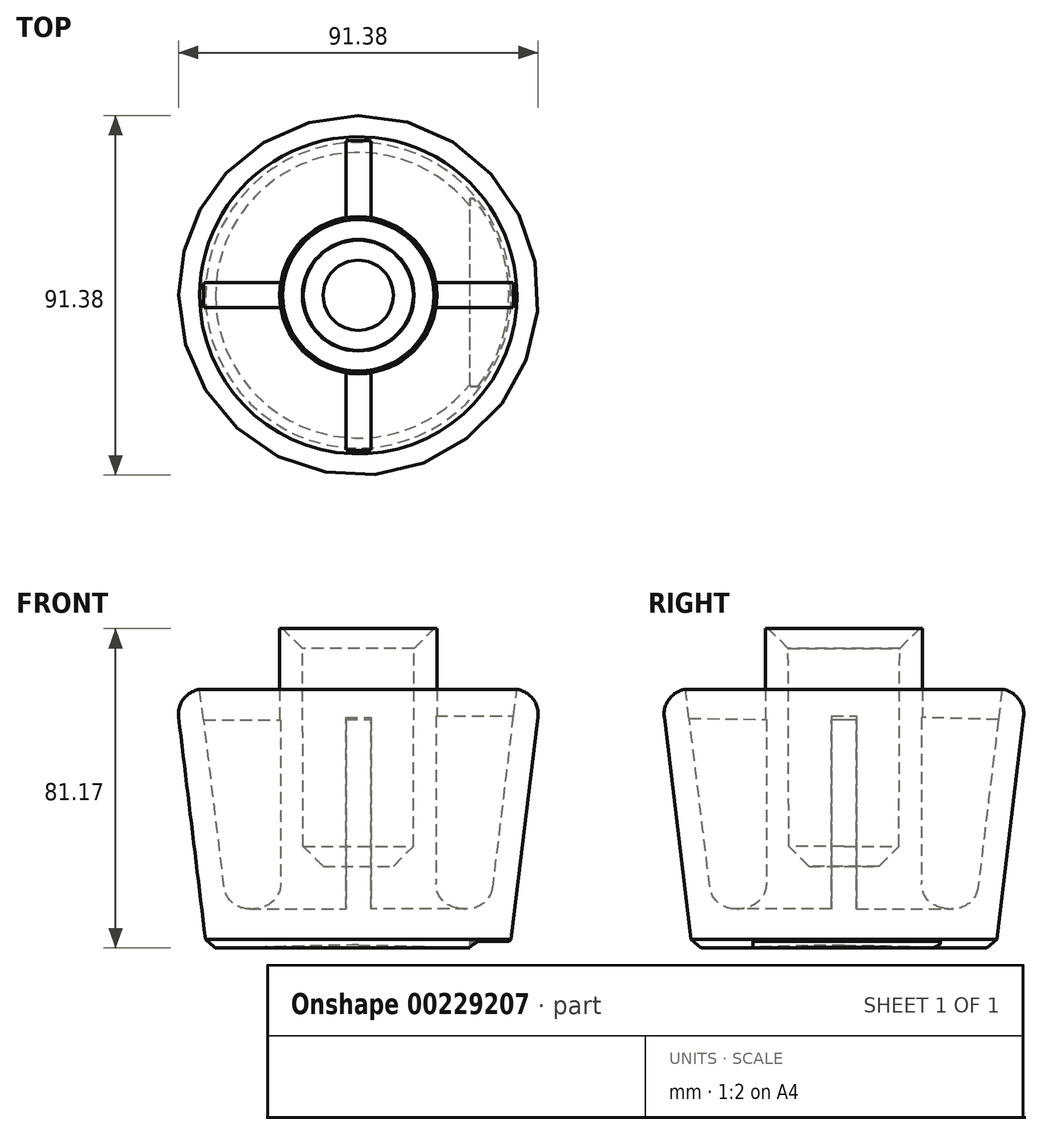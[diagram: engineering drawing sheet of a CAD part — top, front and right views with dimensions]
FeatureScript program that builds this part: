
annotation { "Feature Type Name" : "Feature", "Feature Type Description" : "" }
export const myFeature = defineFeature(function(context is Context, id is Id, definition is map)
    precondition{}
    {
        {
            var Q0;
            Q0=qCreatedBy(makeId("Front.planeOp"),FACE);
            var sketch = newSketch(context, id + "F0", { "sketchPlane" : qUnion([Q0])});
            skLineSegment(sketch, "E0", {"start": v(0, 0) * mm, "end": v(0, 19.05) * mm});
            skLineSegment(sketch, "E1", {"start": v(14.19, 79.46) * mm, "end": v(19.96, 79.46) * mm});
            skLineSegment(sketch, "E2", {"start": v(19.96, 79.46) * mm, "end": v(19.96, 28.66) * mm});
            skLineSegment(sketch, "E3.top", {"start": v(0, 19.05) * mm, "end": v(13.97, 19.05) * mm});
            skLineSegment(sketch, "E3.right", {"start": v(14.19, 79.46) * mm, "end": v(13.97, 19.05) * mm});
            skLineSegment(sketch, "E4", {"start": v(0, 0) * mm, "end": v(0, -0.91) * mm});
            skLineSegment(sketch, "E5", {"start": v(19.96, 28.66) * mm, "end": v(19.96, 14.73) * mm});
            skLineSegment(sketch, "E6", {"start": v(34.24, 13.83) * mm, "end": v(40.28, 64.03) * mm});
            skLineSegment(sketch, "E7", {"start": v(40.1, 64.05) * mm, "end": v(40.28, 64.03) * mm});
            skLineSegment(sketch, "E8", {"start": v(45.64, 56.99) * mm, "end": v(38.57, -1.76) * mm});
            skLineSegment(sketch, "E9", {"start": v(38.57, -1.76) * mm, "end": v(0, -0.91) * mm});
            skPoint(sketch, "E10.visualSharp", {"position": v(46.4, 63.3) * mm});
            skArc(sketch, "E10.filletArc", {"start": v(45.64, 56.99) * mm, "mid": v(44.33, 61.67) * mm, "end": v(40.1, 64.05) * mm});
            skLineSegment(sketch, "E11", {"start": v(27.4, 8.26) * mm, "end": v(25.78, 8.4) * mm});
            skPoint(sketch, "E12.visualSharp", {"position": v(33.5, 7.75) * mm});
            skArc(sketch, "E12.filletArc", {"start": v(27.4, 8.26) * mm, "mid": v(31.94, 9.67) * mm, "end": v(34.24, 13.83) * mm});
            skPoint(sketch, "E13.visualSharp", {"position": v(19.96, 8.9) * mm});
            skArc(sketch, "E13.filletArc", {"start": v(19.96, 14.73) * mm, "mid": v(21.63, 10.43) * mm, "end": v(25.78, 8.4) * mm});
            skSolve(sketch);
        }
        {
            var Q0;
            Q0=makeQuery(id+"F0.imprint","IMPRINT",FACE,{"disambiguationData":[TD([[makeQuery(id+"F0.imprint","IMPRINT",EDGE,{"derivedFrom":sQuery(id+"F0.wireOp",EDGE,"E0")}),-1.0]])]});
            var Q1;
            Q1=sQuery(id+"F0.wireOp",EDGE,"E0");
            revolve(context, id + "F1", {"entities" : qUnion([Q0]), "axis" : qUnion([Q1]), "revolveType" : RevolveType.FULL});
        }
        {
            var Q0;
            Q0=qCreatedBy(makeId("Front.planeOp"),FACE);
            var sketch = newSketch(context, id + "F2", { "sketchPlane" : qUnion([Q0])});
            skLineSegment(sketch, "E14", {"start": v(-40.93, 56.3) * mm, "end": v(-17.64, 56.3) * mm});
            skLineSegment(sketch, "E15", {"start": v(-17.64, 56.3) * mm, "end": v(-17.64, 1.88) * mm});
            skLineSegment(sketch, "E16", {"start": v(-40.93, 56.3) * mm, "end": v(-36.2, 2.28) * mm});
            skLineSegment(sketch, "E17", {"start": v(-36.2, 2.28) * mm, "end": v(-17.64, 1.88) * mm});
            skLineSegment(sketch, "E18", {"start": v(-36.2, 2.28) * mm, "end": v(-36.21, 2.43) * mm});
            skSolve(sketch);
        }
        {
            var Q0;
            Q0=makeQuery(id+"F2.imprint","IMPRINT",FACE,{"disambiguationData":[TD([[makeQuery(id+"F2.imprint","IMPRINT",EDGE,{"derivedFrom":sQuery(id+"F2.wireOp",EDGE,"E14")}),-1.0]])]});
            extrude(context, id + "F3", {"entities" : qUnion([Q0]), "operationType" : NewBodyOperationType.ADD, "endBound" : BoundingType.SYMMETRIC, "depth" : 6.35 * mm});
        }
        {
            var Q0;
            Q0=qCreatedBy(makeId("Front.planeOp"),FACE);
            var sketch = newSketch(context, id + "F4", { "sketchPlane" : qUnion([Q0])});
            skLineSegment(sketch, "E19", {"start": v(16.79, 57.32) * mm, "end": v(42.76, 57.32) * mm});
            skLineSegment(sketch, "E20", {"start": v(42.76, 57.32) * mm, "end": v(35.94, 0.2) * mm});
            skLineSegment(sketch, "E21", {"start": v(35.94, 0.2) * mm, "end": v(16.79, 0.2) * mm});
            skLineSegment(sketch, "E22", {"start": v(16.79, 0.2) * mm, "end": v(16.79, 57.32) * mm});
            skSolve(sketch);
        }
        {
            var Q0;
            Q0=makeQuery(id+"F4.imprint","IMPRINT",FACE,{"disambiguationData":[TD([[makeQuery(id+"F4.imprint","IMPRINT",EDGE,{"derivedFrom":sQuery(id+"F4.wireOp",EDGE,"E19")}),-1.0]])]});
            extrude(context, id + "F5", {"entities" : qUnion([Q0]), "operationType" : NewBodyOperationType.ADD, "endBound" : BoundingType.SYMMETRIC, "depth" : 6.35 * mm});
        }
        {
            var Q0;
            Q0=qCreatedBy(makeId("Right.planeOp"),FACE);
            var sketch = newSketch(context, id + "F6", { "sketchPlane" : qUnion([Q0])});
            skLineSegment(sketch, "E23", {"start": v(-16.43, 56.32) * mm, "end": v(-16.43, 1.24) * mm});
            skLineSegment(sketch, "E24", {"start": v(-16.43, 1.24) * mm, "end": v(-34.4, 1.24) * mm});
            skLineSegment(sketch, "E25", {"start": v(-34.4, 1.24) * mm, "end": v(-41, 56.65) * mm});
            skLineSegment(sketch, "E26", {"start": v(-41, 56.65) * mm, "end": v(-16.43, 56.32) * mm});
            skLineSegment(sketch, "E27", {"start": v(17.86, 56.9) * mm, "end": v(17.86, 0.03) * mm});
            skLineSegment(sketch, "E28", {"start": v(17.86, 0.03) * mm, "end": v(35.46, -0.2) * mm});
            skLineSegment(sketch, "E29", {"start": v(35.46, -0.2) * mm, "end": v(42.7, 56.24) * mm});
            skLineSegment(sketch, "E30", {"start": v(42.7, 56.24) * mm, "end": v(17.86, 56.9) * mm});
            skSolve(sketch);
        }
        {
            var Q0;
            Q0=makeQuery(id+"F6.imprint","IMPRINT",FACE,{"disambiguationData":[TD([[makeQuery(id+"F6.imprint","IMPRINT",EDGE,{"derivedFrom":sQuery(id+"F6.wireOp",EDGE,"E23")}),-1.0]])]});
            var Q1;
            Q1=makeQuery(id+"F6.imprint","IMPRINT",FACE,{"disambiguationData":[TD([[makeQuery(id+"F6.imprint","IMPRINT",EDGE,{"derivedFrom":sQuery(id+"F6.wireOp",EDGE,"E27")}),1.0]])]});
            extrude(context, id + "F7", {"entities" : qUnion([Q0, Q1]), "operationType" : NewBodyOperationType.ADD, "endBound" : BoundingType.SYMMETRIC, "depth" : 6.35 * mm});
        }
        {
            var Q0;
            Q0=makeQuery(id+"F1.opRevolve","SWEPT_EDGE",EDGE,{"disambiguationData":[OSD([sQuery(id+"F0.wireOp",EDGE,"E8"),sQuery(id+"F0.wireOp",EDGE,"E9")])]});
            chamfer(context, id + "F8", {"entities" : qUnion([Q0]), "width" : 2.54 * mm, "tangentPropagation" : true});
        }
        {
            var Q0;
            Q0=makeQuery(id+"F1.opRevolve","SWEPT_FACE",FACE,{"disambiguationData":[OSD([sQuery(id+"F0.wireOp",EDGE,"E3.right")])]});
            chamfer(context, id + "F9", {"entities" : qUnion([Q0]), "width" : 5.08 * mm, "tangentPropagation" : true});
        }
        {
            var Q0;
            Q0=qCreatedBy(makeId("Top.planeOp"),FACE);
            var sketch = newSketch(context, id + "F10", { "sketchPlane" : qUnion([Q0])});
            skLineSegment(sketch, "E31.bottom", {"start": v(40.84, -23.15) * mm, "end": v(28.32, -23.15) * mm});
            skLineSegment(sketch, "E31.top", {"start": v(40.84, 24.51) * mm, "end": v(28.32, 24.51) * mm});
            skLineSegment(sketch, "E31.left", {"start": v(40.84, -23.15) * mm, "end": v(40.84, 24.51) * mm});
            skLineSegment(sketch, "E31.right", {"start": v(28.32, -23.15) * mm, "end": v(28.32, 24.51) * mm});
            skSolve(sketch);
        }
        {
            var Q0;
            Q0=makeQuery(id+"F10.imprint","IMPRINT",FACE,{"disambiguationData":[TD([[makeQuery(id+"F10.imprint","IMPRINT",EDGE,{"derivedFrom":sQuery(id+"F10.wireOp",EDGE,"E31.bottom")}),-1.0]])]});
            extrude(context, id + "F11", {"entities" : qUnion([Q0]), "operationType" : NewBodyOperationType.REMOVE, "oppositeDirection" : true, "depth" : 25.4 * mm});
        }
    });
